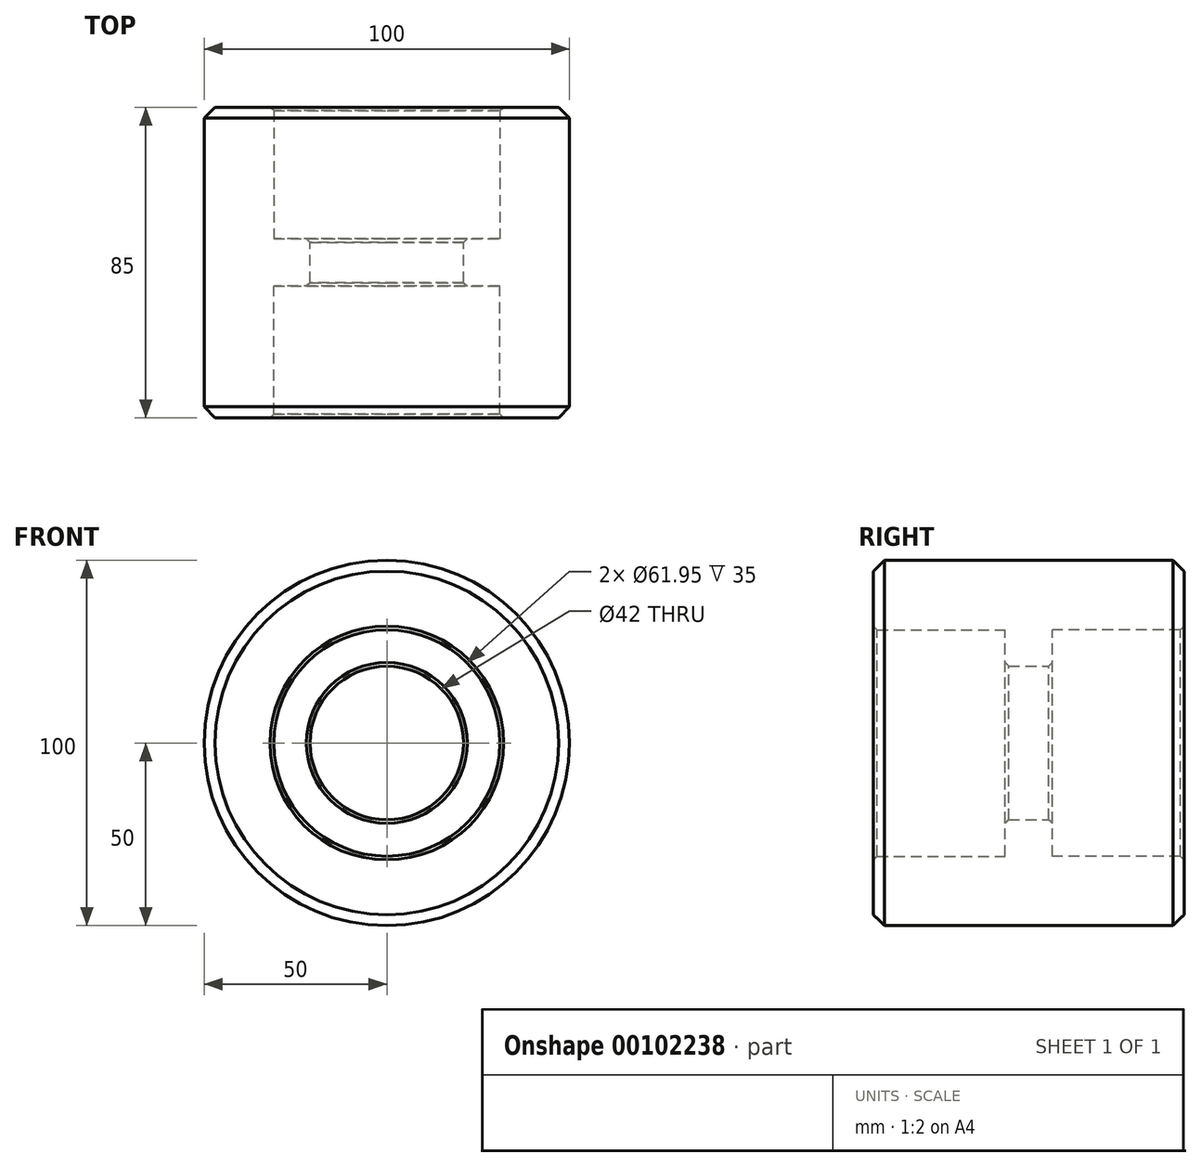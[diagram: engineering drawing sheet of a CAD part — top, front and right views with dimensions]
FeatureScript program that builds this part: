
annotation { "Feature Type Name" : "Feature", "Feature Type Description" : "" }
export const myFeature = defineFeature(function(context is Context, id is Id, definition is map)
    precondition{}
    {
        {
            var Q0;
            Q0=qCreatedBy(makeId("Front.planeOp"),FACE);
            var sketch = newSketch(context, id + "F0", { "sketchPlane" : qUnion([Q0])});
            skCircle(sketch, "E0", {"center": v(0, 0) * mm, "radius": 21 * mm});
            skCircle(sketch, "E1", {"center": v(0, 0) * mm, "radius": 30.98 * mm});
            skCircle(sketch, "E2", {"center": v(0, 0) * mm, "radius": 50 * mm});
            skSolve(sketch);
        }
        {
            var Q0;
            Q0=makeQuery(id+"F0.imprint","IMPRINT",FACE,{"disambiguationData":[TD([[makeQuery(id+"F0.imprint","IMPRINT",EDGE,{"derivedFrom":sQuery(id+"F0.wireOp",EDGE,"E0")}),-1.0]])]});
            extrude(context, id + "F1", {"entities" : qUnion([Q0]), "endBound" : BoundingType.SYMMETRIC, "depth" : 13 * mm});
        }
        {
            var Q0;
            Q0 = qSketchRegion(id + "F0", true);
            extrude(context, id + "F2", {"entities" : qUnion([Q0]), "operationType" : NewBodyOperationType.ADD, "depth" : 42.5 * mm});
        }
        {
            var Q0;
            Q0=makeQuery(id+"F2.opExtrude","CAP_FACE",FACE,{"disambiguationData":[OSD([sQuery(id+"F0.wireOp",EDGE,"E1"),sQuery(id+"F0.wireOp",EDGE,"E2")])],"isStart":true});
            extrude(context, id + "F3", {"entities" : qUnion([Q0]), "operationType" : NewBodyOperationType.ADD, "depth" : 42.5 * mm});
        }
        {
            var Q0;
            Q0=makeQuery(id+"F3.opExtrude","CAP_EDGE",EDGE,{"disambiguationData":[OSD([sQuery(id+"F0.wireOp",EDGE,"E2")])],"isStart":false});
            var Q1;
            Q1=makeQuery(id+"F2.opExtrude","CAP_EDGE",EDGE,{"disambiguationData":[OSD([sQuery(id+"F0.wireOp",EDGE,"E2")])],"isStart":false});
            chamfer(context, id + "F4", {"entities" : qUnion([Q0, Q1]), "width" : 3 * mm, "tangentPropagation" : true});
        }
        {
            var Q0;
            Q0=makeQuery(id+"F3.opExtrude","CAP_EDGE",EDGE,{"disambiguationData":[OSD([sQuery(id+"F0.wireOp",EDGE,"E1")])],"isStart":false});
            var Q1;
            Q1=makeQuery(id+"F1.opExtrude","CAP_EDGE",EDGE,{"disambiguationData":[OSD([sQuery(id+"F0.wireOp",EDGE,"E0")])],"isStart":true});
            var Q2;
            Q2=makeQuery(id+"F1.opExtrude","CAP_EDGE",EDGE,{"disambiguationData":[OSD([sQuery(id+"F0.wireOp",EDGE,"E0")])],"isStart":false});
            var Q3;
            Q3=makeQuery(id+"F2.opExtrude","CAP_EDGE",EDGE,{"disambiguationData":[OSD([sQuery(id+"F0.wireOp",EDGE,"E1")])],"isStart":false});
            chamfer(context, id + "F5", {"entities" : qUnion([Q0, Q1, Q2, Q3]), "width" : 1 * mm, "tangentPropagation" : true});
        }
    });
